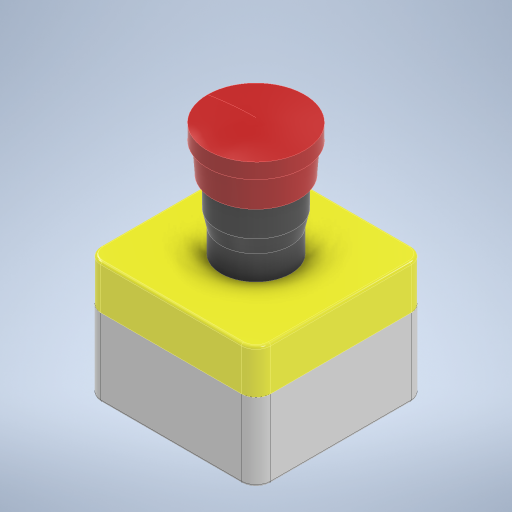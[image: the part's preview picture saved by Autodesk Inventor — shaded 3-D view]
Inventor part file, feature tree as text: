
AUTODESK INVENTOR PART (.ipt)
format: ipt  version: 2023 (Build 270158030, 158C)  size: 426,496 bytes
history: native  units: mm
features: sketch x11, extrude x10, projected_geometry x5, fillet x4, other x3, revolve x1
ambient origin geometry x8: Origin, YZ Plane, XZ Plane, XY Plane, X Axis, Y Axis, Z Axis, Center Point
bodies: Solid1 (feature_tree)
feature tree (34):
  extrude  "Extrusion1"  Depth=69.6mm
  extrude  "Extrusion2"  Depth=34.825mm
  fillet  "Fillet1"  Radius=4.6mm
  fillet  "Fillet2"  Radius=17.0mm
  fillet  "Fillet3"  Radius=6.0mm
  extrude  "Extrusion3"  Depth=17.0mm
  extrude  "Extrusion4"  Depth=1.12mm
  fillet  "Fillet4"  Radius=29.4mm
  extrude  "Extrusion5"  Depth=5.0mm
  extrude  "Extrusion6"  Depth=1.0mm TaperAngle=0.0deg
  extrude  "Extrusion7"  Depth=1.0mm
  extrude  "Extrusion8"  Depth=10.0mm TaperAngle=0.0deg
  revolve  "Revolution1"  [1 undecoded]
  extrude  "Extrusion10"  Depth=12.0mm
  extrude  "Extrusion9"  Depth=1.0mm TaperAngle=0.0deg
  sketch  "Sketch1"  dims[d0=69.65mm d1=69.6mm]
  sketch  "Sketch2"  dims[d2=34.8mm d3=34.825mm d4=4.6mm d5=17.0mm d6=6.0mm]
  projected_geometry  "Projected Loop1"
  sketch  "Sketch3"  dims[d7=6.0mm d8=17.0mm]
  projected_geometry  "Projected Loop2"
  other  "yellow"
  sketch  "Sketch4"  dims[d9=2.6mm d10=0.0mm d11=1.12mm d12=29.4mm d13=0.0mm]
  projected_geometry  "Projected Loop3"
  sketch  "Sketch5"  dims[d14=5.0mm d15=6.0mm]
  other  "black"
  sketch  "Sketch6"  dims[d16=1.0mm d17=18.0mm d18=0.0mm]
  projected_geometry  "Projected Loop4"
  sketch  "Sketch7"  dims[d19=1.1mm d20=0.0mm d21=1.0mm]
  projected_geometry  "Projected Loop5"
  sketch  "Sketch8"  dims[d22=28.6mm d23=10.0mm d24=0.0mm]
  other  "red"
  sketch  "Sketch9"  dims[d25=6.26mm d26=2.094395mm d27=12.0mm d28=0.0mm]
  sketch  "Sketch10"  dims[d29=35.5mm d30=12.0mm d31=0.698132mm]
  sketch  "Sketch11"  dims[d32=39.6mm d33=8.0mm d34=0.0mm d35=19.85mm d36=6.26mm d37=8.0mm d38=9.0mm d39=360.0deg d40=19.0mm d41=15.0mm d42=15.0mm d43=1.0mm d44=0.0mm]
note: 1 required parameter value undecoded (feature->parameter linkage not recoverable at this tier; creation-order binding heuristic only, values carry confidence <= 0.55)
